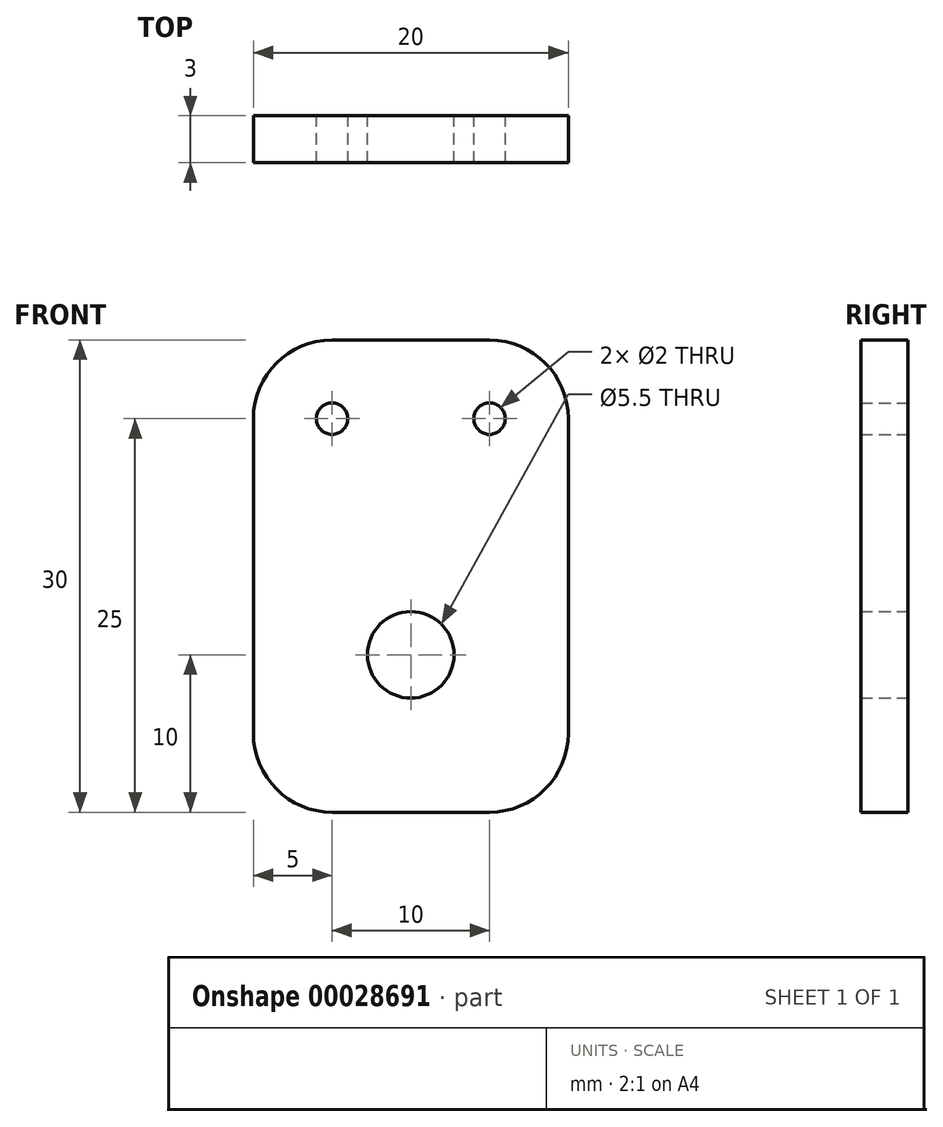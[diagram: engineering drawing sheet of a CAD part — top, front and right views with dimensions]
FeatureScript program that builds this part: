
annotation { "Feature Type Name" : "Feature", "Feature Type Description" : "" }
export const myFeature = defineFeature(function(context is Context, id is Id, definition is map)
    precondition{}
    {
        {
            var Q0;
            Q0=qCreatedBy(makeId("Front.planeOp"),FACE);
            var sketch = newSketch(context, id + "F0", { "sketchPlane" : qUnion([Q0])});
            skLineSegment(sketch, "E0.bottom", {"start": v(5, 0) * mm, "end": v(15, 0) * mm});
            skLineSegment(sketch, "E0.top", {"start": v(5, 30) * mm, "end": v(15, 30) * mm});
            skLineSegment(sketch, "E0.left", {"start": v(0, 5) * mm, "end": v(0, 25) * mm});
            skLineSegment(sketch, "E0.right", {"start": v(20, 5) * mm, "end": v(20, 25) * mm});
            skCircle(sketch, "E1", {"center": v(10, 10) * mm, "radius": 2.75 * mm});
            skLineSegment(sketch, "E2", {"start": v(10, 10) * mm, "end": v(10, 0) * mm, "construction": true});
            skLineSegment(sketch, "E3", {"start": v(10, 10) * mm, "end": v(0, 10) * mm, "construction": true});
            skCircle(sketch, "E4", {"center": v(5, 25) * mm, "radius": 1 * mm});
            skCircle(sketch, "E5", {"center": v(15, 25) * mm, "radius": 1 * mm});
            skLineSegment(sketch, "E6", {"start": v(5, 25) * mm, "end": v(0, 25) * mm, "construction": true});
            skLineSegment(sketch, "E7", {"start": v(15, 25) * mm, "end": v(20, 25) * mm, "construction": true});
            skLineSegment(sketch, "E8", {"start": v(5, 25) * mm, "end": v(15, 25) * mm, "construction": true});
            skLineSegment(sketch, "E9", {"start": v(10, 25) * mm, "end": v(10, 30) * mm, "construction": true});
            skPoint(sketch, "E10.visualSharp", {"position": v(0, 30) * mm});
            skArc(sketch, "E10.filletArc", {"start": v(5, 30) * mm, "mid": v(1.46, 28.54) * mm, "end": v(0, 25) * mm});
            skPoint(sketch, "E11.visualSharp", {"position": v(20, 30) * mm});
            skArc(sketch, "E11.filletArc", {"start": v(20, 25) * mm, "mid": v(18.54, 28.54) * mm, "end": v(15, 30) * mm});
            skPoint(sketch, "E12.visualSharp", {"position": v(20, 0) * mm});
            skArc(sketch, "E12.filletArc", {"start": v(15, 0) * mm, "mid": v(18.54, 1.46) * mm, "end": v(20, 5) * mm});
            skPoint(sketch, "E13.visualSharp", {"position": v(0, 0) * mm});
            skArc(sketch, "E13.filletArc", {"start": v(0, 5) * mm, "mid": v(1.46, 1.46) * mm, "end": v(5, 0) * mm});
            skSolve(sketch);
        }
        {
            var Q0;
            Q0 = qSketchRegion(id + "F0", true);
            extrude(context, id + "F1", {"entities" : qUnion([Q0]), "depth" : 3 * mm});
        }
    });
